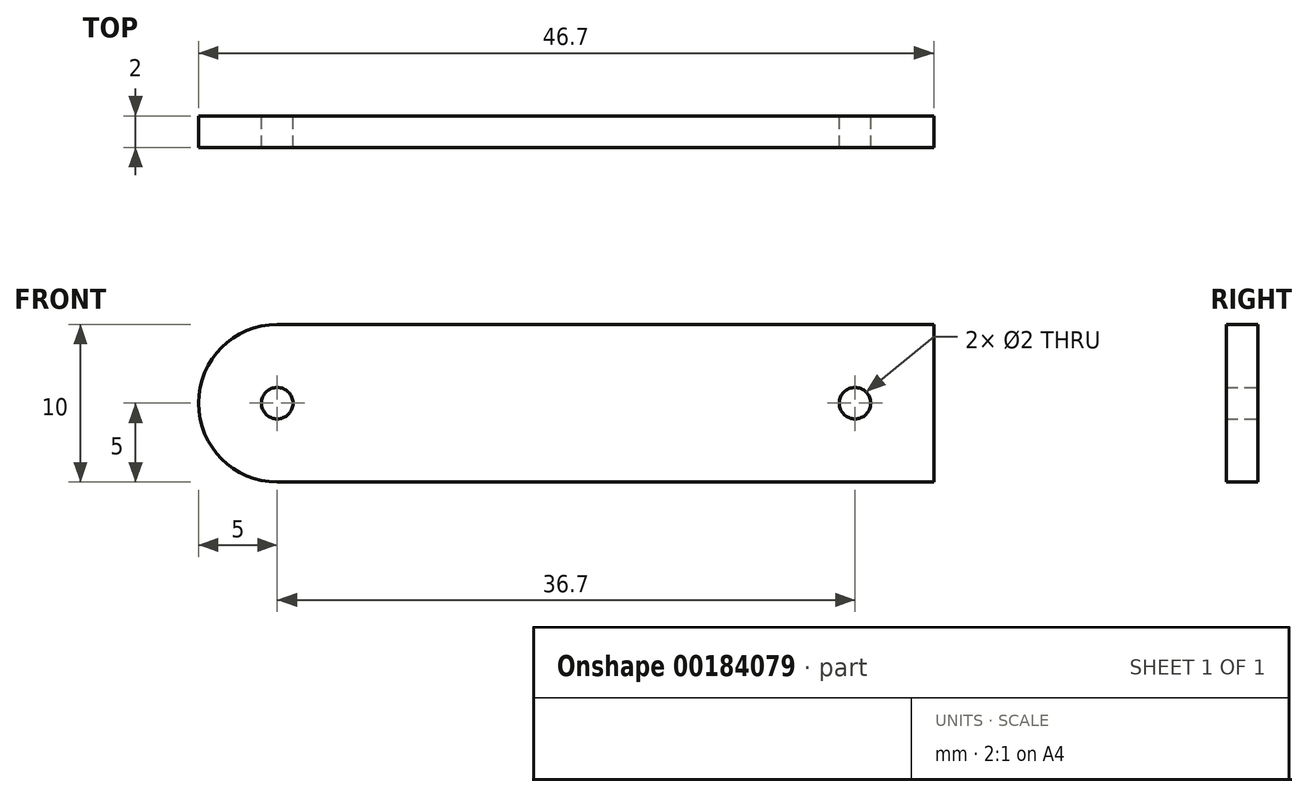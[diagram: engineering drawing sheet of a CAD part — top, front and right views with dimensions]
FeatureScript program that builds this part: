
annotation { "Feature Type Name" : "Feature", "Feature Type Description" : "" }
export const myFeature = defineFeature(function(context is Context, id is Id, definition is map)
    precondition{}
    {
        {
            var Q0;
            Q0=qCreatedBy(makeId("Front.planeOp"),FACE);
            var sketch = newSketch(context, id + "F0", { "sketchPlane" : qUnion([Q0])});
            skLineSegment(sketch, "E0.bottom", {"start": v(0, 0) * mm, "end": v(41.7, 0) * mm});
            skLineSegment(sketch, "E0.top", {"start": v(0, -10) * mm, "end": v(41.7, -10) * mm});
            skLineSegment(sketch, "E0.right", {"start": v(41.7, 0) * mm, "end": v(41.7, -10) * mm});
            skArc(sketch, "E1", {"start": v(0, 0) * mm, "mid": v(-5, -5) * mm, "end": v(0, -10) * mm});
            skCircle(sketch, "E2", {"center": v(0, -5) * mm, "radius": 1 * mm});
            skCircle(sketch, "E3", {"center": v(36.7, -5) * mm, "radius": 1 * mm});
            skSolve(sketch);
        }
        {
            var Q0;
            Q0 = qSketchRegion(id + "F0", true);
            extrude(context, id + "F1", {"entities" : qUnion([Q0]), "depth" : 2 * mm});
        }
    });
